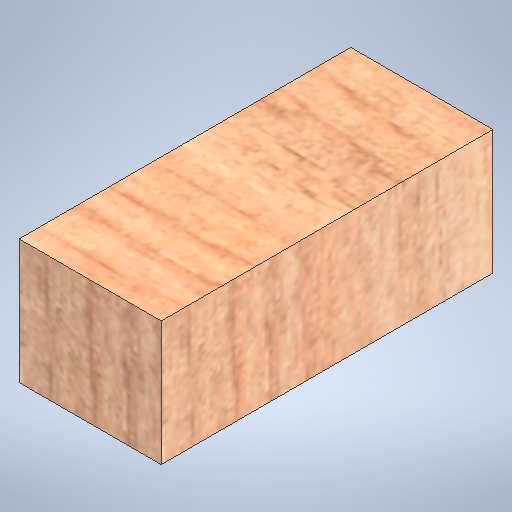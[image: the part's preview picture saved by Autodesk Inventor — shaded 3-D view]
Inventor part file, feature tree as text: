
AUTODESK INVENTOR PART (.ipt)
format: ipt  version: 2025.1 (Build 291241020, 241B)  size: 479,232 bytes
history: native  units: in
note: dims shown in document units (in); Inventor stores cm internally (conversion verified against a paired STEP export)
features: extrude x1, sketch x1
ambient origin geometry x8: Origin, YZ Plane, XZ Plane, XY Plane, X Axis, Y Axis, Z Axis, Center Point
bodies: Solid1 (feature_tree)
feature tree (2):
  extrude  "Extrusion1"  Depth=1.5in
  sketch  "Sketch1"  dims[d0=3.5in d1=1.5in d2=1.3125in d3=0.0in]
